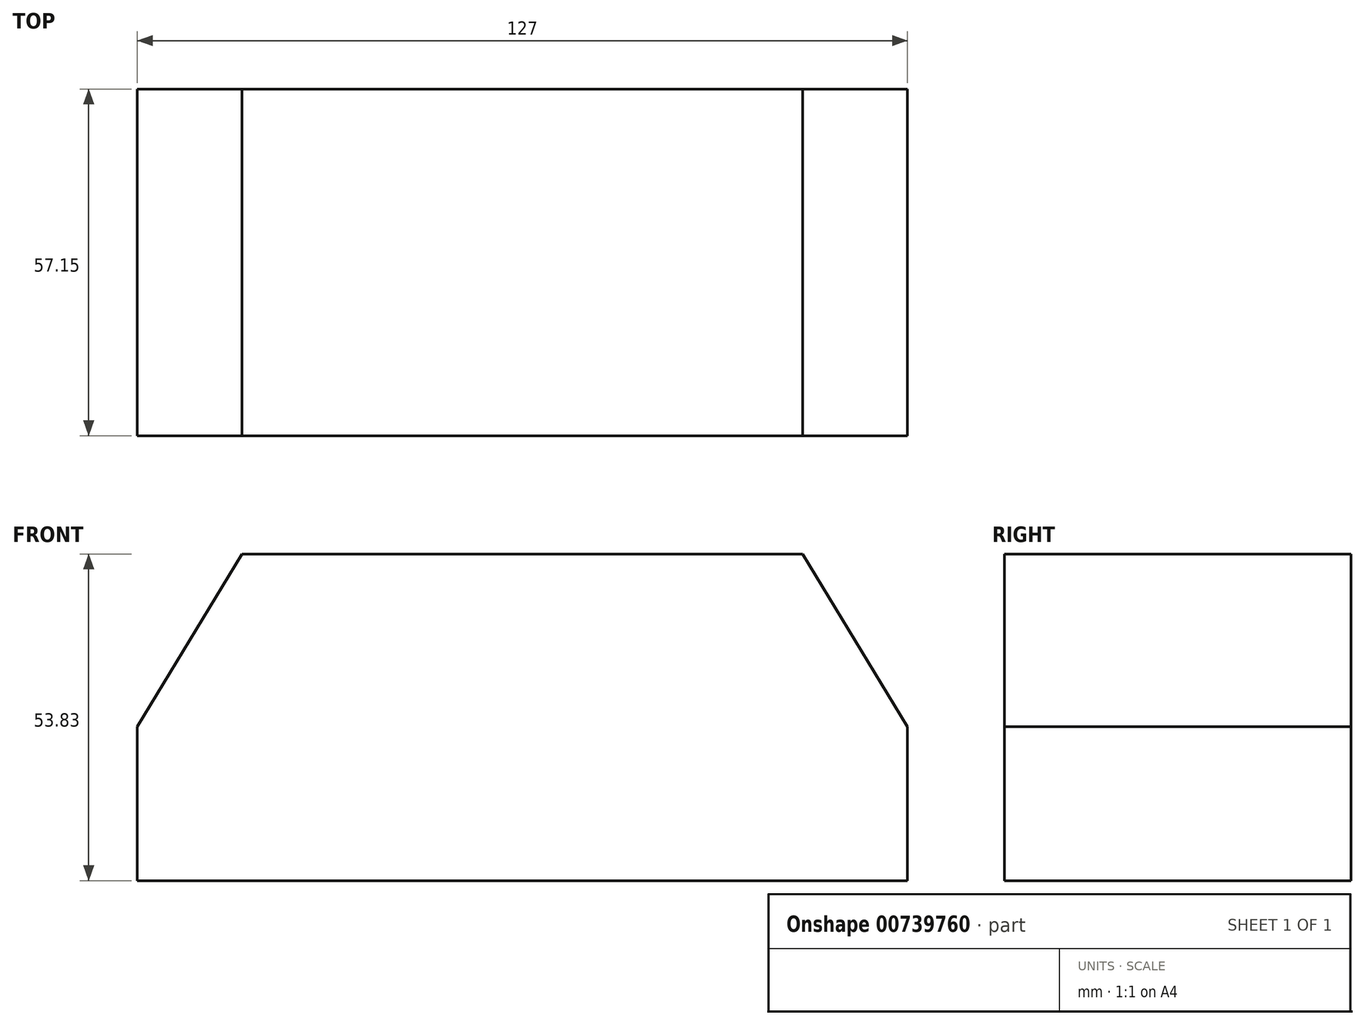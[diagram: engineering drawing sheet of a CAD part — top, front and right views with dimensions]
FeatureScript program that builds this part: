
annotation { "Feature Type Name" : "Feature", "Feature Type Description" : "" }
export const myFeature = defineFeature(function(context is Context, id is Id, definition is map)
    precondition{}
    {
        {
            var Q0;
            Q0=qCreatedBy(makeId("Front.planeOp"),FACE);
            var sketch = newSketch(context, id + "F0", { "sketchPlane" : qUnion([Q0])});
            skLineSegment(sketch, "E0", {"start": v(-54.48, -53.83) * mm, "end": v(72.52, -53.83) * mm});
            skLineSegment(sketch, "E1", {"start": v(72.52, -53.83) * mm, "end": v(72.52, -28.43) * mm});
            skLineSegment(sketch, "E2", {"start": v(72.52, -28.43) * mm, "end": v(55.24, 0) * mm});
            skLineSegment(sketch, "E3", {"start": v(55.24, 0) * mm, "end": v(-37.2, 0) * mm});
            skLineSegment(sketch, "E4", {"start": v(-54.48, -53.83) * mm, "end": v(-54.48, -28.43) * mm});
            skLineSegment(sketch, "E5", {"start": v(-54.48, -28.43) * mm, "end": v(-37.2, 0) * mm});
            skSolve(sketch);
        }
        {
            var Q0;
            Q0=makeQuery(id+"F0.imprint","IMPRINT",FACE,{"disambiguationData":[TD([[makeQuery(id+"F0.imprint","IMPRINT",EDGE,{"derivedFrom":sQuery(id+"F0.wireOp",EDGE,"E0")}),1.0]])]});
            extrude(context, id + "F1", {"entities" : qUnion([Q0]), "depth" : 57.15 * mm, "offsetDistance" : 25.4 * mm});
        }
    });
